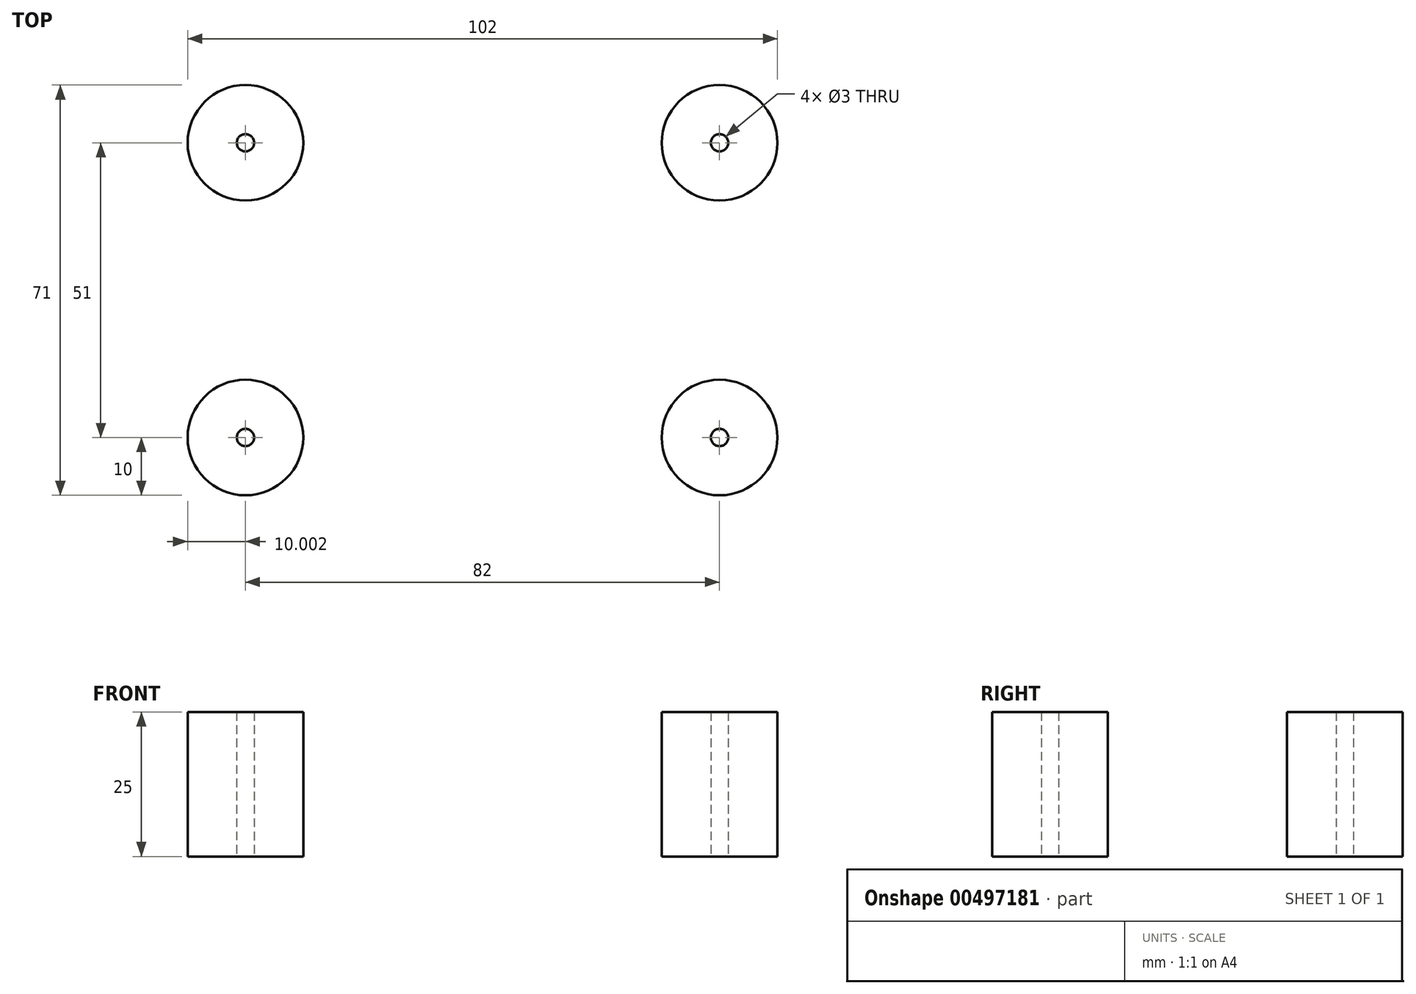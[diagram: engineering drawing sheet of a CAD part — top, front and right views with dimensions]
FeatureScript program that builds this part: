
annotation { "Feature Type Name" : "Feature", "Feature Type Description" : "" }
export const myFeature = defineFeature(function(context is Context, id is Id, definition is map)
    precondition{}
    {
        {
            var Q0;
            Q0=qCreatedBy(makeId("Top.planeOp"),FACE);
            var sketch = newSketch(context, id + "F0", { "sketchPlane" : qUnion([Q0])});
            skLineSegment(sketch, "E0.bottom", {"start": v(-75.58, 100.07) * mm, "end": v(74.42, 100.07) * mm});
            skLineSegment(sketch, "E0.top", {"start": v(-75.58, -99.93) * mm, "end": v(74.42, -99.93) * mm});
            skLineSegment(sketch, "E0.left", {"start": v(-75.58, 100.07) * mm, "end": v(-75.58, -99.93) * mm});
            skLineSegment(sketch, "E0.right", {"start": v(74.42, 100.07) * mm, "end": v(74.42, -99.93) * mm});
            skPoint(sketch, "E0.middle", {"position": v(-0.58, 0.07) * mm});
            skLineSegment(sketch, "E1.bottom", {"start": v(-69.33, 93.82) * mm, "end": v(68.17, 93.82) * mm});
            skLineSegment(sketch, "E1.top", {"start": v(-69.33, -93.68) * mm, "end": v(68.17, -93.68) * mm});
            skLineSegment(sketch, "E1.left", {"start": v(-69.33, 93.82) * mm, "end": v(-69.33, -93.68) * mm});
            skLineSegment(sketch, "E1.right", {"start": v(68.17, 93.82) * mm, "end": v(68.17, -93.68) * mm});
            skLineSegment(sketch, "E2.bottom", {"start": v(-63.08, 87.57) * mm, "end": v(61.92, 87.57) * mm});
            skLineSegment(sketch, "E2.top", {"start": v(-63.08, -87.43) * mm, "end": v(61.92, -87.43) * mm});
            skLineSegment(sketch, "E2.left", {"start": v(-63.08, 87.57) * mm, "end": v(-63.08, -87.43) * mm});
            skLineSegment(sketch, "E2.right", {"start": v(61.92, 87.57) * mm, "end": v(61.92, -87.43) * mm});
            skLineSegment(sketch, "E3.bottom", {"start": v(-51.58, 35.57) * mm, "end": v(50.42, 35.57) * mm, "construction": true});
            skLineSegment(sketch, "E3.top", {"start": v(-51.58, -35.43) * mm, "end": v(50.42, -35.43) * mm, "construction": true});
            skLineSegment(sketch, "E3.left", {"start": v(-51.58, 35.57) * mm, "end": v(-51.58, -35.43) * mm, "construction": true});
            skLineSegment(sketch, "E3.right", {"start": v(50.42, 35.57) * mm, "end": v(50.42, -35.43) * mm, "construction": true});
            skPoint(sketch, "E4", {"position": v(36.92, 87.57) * mm});
            skPoint(sketch, "E5", {"position": v(36.92, -87.43) * mm});
            skPoint(sketch, "E6", {"position": v(-38.08, 87.57) * mm});
            skPoint(sketch, "E7", {"position": v(-38.08, -87.43) * mm});
            skPoint(sketch, "E8", {"position": v(-63.08, 62.57) * mm});
            skPoint(sketch, "E9", {"position": v(61.92, 62.57) * mm});
            skPoint(sketch, "E10", {"position": v(61.92, -62.43) * mm});
            skPoint(sketch, "E11", {"position": v(-63.08, -62.43) * mm});
            skPoint(sketch, "E12", {"position": v(-63.08, 87.57) * mm});
            skPoint(sketch, "E13", {"position": v(61.92, 87.57) * mm});
            skPoint(sketch, "E14", {"position": v(61.92, -87.43) * mm});
            skPoint(sketch, "E15", {"position": v(-63.08, -87.43) * mm});
            skLineSegment(sketch, "E16", {"start": v(-63.08, -62.43) * mm, "end": v(-38.08, -87.43) * mm});
            skLineSegment(sketch, "E17", {"start": v(36.92, -87.43) * mm, "end": v(61.92, -62.43) * mm});
            skLineSegment(sketch, "E18", {"start": v(61.92, 62.57) * mm, "end": v(36.92, 87.57) * mm});
            skLineSegment(sketch, "E19", {"start": v(-38.08, 87.57) * mm, "end": v(-63.08, 62.57) * mm});
            skPoint(sketch, "E20", {"position": v(-50.58, 75.07) * mm});
            skPoint(sketch, "E21", {"position": v(49.42, 75.07) * mm});
            skPoint(sketch, "E22", {"position": v(49.42, -74.93) * mm});
            skPoint(sketch, "E23", {"position": v(-50.58, -74.93) * mm});
            skLineSegment(sketch, "E24", {"start": v(-63.08, 87.57) * mm, "end": v(-50.58, 75.07) * mm, "construction": true});
            skLineSegment(sketch, "E25", {"start": v(61.92, 87.57) * mm, "end": v(49.42, 75.07) * mm, "construction": true});
            skLineSegment(sketch, "E26", {"start": v(61.92, -87.43) * mm, "end": v(49.42, -74.93) * mm, "construction": true});
            skLineSegment(sketch, "E27", {"start": v(-63.08, -87.43) * mm, "end": v(-50.58, -74.93) * mm, "construction": true});
            skPoint(sketch, "E28", {"position": v(-56.83, 81.32) * mm});
            skPoint(sketch, "E29", {"position": v(55.67, 81.32) * mm});
            skPoint(sketch, "E30", {"position": v(55.67, -81.18) * mm});
            skPoint(sketch, "E31", {"position": v(-56.83, -81.18) * mm});
            skLineSegment(sketch, "E32.bottom", {"start": v(-51.58, 35.57) * mm, "end": v(-41.58, 35.57) * mm, "construction": true});
            skLineSegment(sketch, "E32.top", {"start": v(-51.58, 25.57) * mm, "end": v(-41.58, 25.57) * mm, "construction": true});
            skLineSegment(sketch, "E32.left", {"start": v(-51.58, 35.57) * mm, "end": v(-51.58, 25.57) * mm, "construction": true});
            skLineSegment(sketch, "E32.right", {"start": v(-41.58, 35.57) * mm, "end": v(-41.58, 25.57) * mm, "construction": true});
            skLineSegment(sketch, "E33.bottom", {"start": v(50.42, 35.57) * mm, "end": v(40.42, 35.57) * mm, "construction": true});
            skLineSegment(sketch, "E33.top", {"start": v(50.42, 25.57) * mm, "end": v(40.42, 25.57) * mm, "construction": true});
            skLineSegment(sketch, "E33.left", {"start": v(50.42, 35.57) * mm, "end": v(50.42, 25.57) * mm, "construction": true});
            skLineSegment(sketch, "E33.right", {"start": v(40.42, 35.57) * mm, "end": v(40.42, 25.57) * mm, "construction": true});
            skLineSegment(sketch, "E34.bottom", {"start": v(-51.58, -35.43) * mm, "end": v(-41.58, -35.43) * mm, "construction": true});
            skLineSegment(sketch, "E34.top", {"start": v(-51.58, -25.43) * mm, "end": v(-41.58, -25.43) * mm, "construction": true});
            skLineSegment(sketch, "E34.left", {"start": v(-51.58, -35.43) * mm, "end": v(-51.58, -25.43) * mm, "construction": true});
            skLineSegment(sketch, "E34.right", {"start": v(-41.58, -35.43) * mm, "end": v(-41.58, -25.43) * mm, "construction": true});
            skLineSegment(sketch, "E35.bottom", {"start": v(50.42, -35.43) * mm, "end": v(40.42, -35.43) * mm, "construction": true});
            skLineSegment(sketch, "E35.top", {"start": v(50.42, -25.43) * mm, "end": v(40.42, -25.43) * mm, "construction": true});
            skLineSegment(sketch, "E35.left", {"start": v(50.42, -35.43) * mm, "end": v(50.42, -25.43) * mm, "construction": true});
            skLineSegment(sketch, "E35.right", {"start": v(40.42, -35.43) * mm, "end": v(40.42, -25.43) * mm, "construction": true});
            skPoint(sketch, "E36", {"position": v(-41.58, 25.57) * mm});
            skPoint(sketch, "E37", {"position": v(40.42, 25.57) * mm});
            skPoint(sketch, "E38", {"position": v(40.42, -25.43) * mm});
            skPoint(sketch, "E39", {"position": v(-41.58, -25.43) * mm});
            skCircle(sketch, "E40", {"center": v(40.42, 25.57) * mm, "radius": 10 * mm});
            skCircle(sketch, "E41", {"center": v(-41.58, 25.57) * mm, "radius": 10 * mm});
            skCircle(sketch, "E42", {"center": v(-41.58, -25.43) * mm, "radius": 10 * mm});
            skCircle(sketch, "E43", {"center": v(40.42, -25.43) * mm, "radius": 10 * mm});
            skCircle(sketch, "E44", {"center": v(40.42, 25.57) * mm, "radius": 1.5 * mm});
            skCircle(sketch, "E45", {"center": v(-41.58, 25.57) * mm, "radius": 1.5 * mm});
            skCircle(sketch, "E46", {"center": v(-41.58, -25.43) * mm, "radius": 1.5 * mm});
            skCircle(sketch, "E47", {"center": v(40.42, -25.43) * mm, "radius": 1.5 * mm});
            skCircle(sketch, "E48", {"center": v(-0.58, 0.07) * mm, "radius": 10 * mm});
            skCircle(sketch, "E49", {"center": v(-63.08, 87.57) * mm, "radius": 1.5 * mm});
            skCircle(sketch, "E50", {"center": v(61.92, 87.57) * mm, "radius": 1.5 * mm});
            skCircle(sketch, "E51", {"center": v(61.92, -87.43) * mm, "radius": 1.5 * mm});
            skCircle(sketch, "E52", {"center": v(-63.08, -87.43) * mm, "radius": 1.5 * mm});
            skCircle(sketch, "E53", {"center": v(-56.83, -81.18) * mm, "radius": 2.5 * mm});
            skCircle(sketch, "E54", {"center": v(55.67, -81.18) * mm, "radius": 2.5 * mm});
            skCircle(sketch, "E55", {"center": v(55.67, 81.32) * mm, "radius": 2.5 * mm});
            skCircle(sketch, "E56", {"center": v(-56.83, 81.32) * mm, "radius": 2.5 * mm});
            skPoint(sketch, "E57", {"position": v(-0.58, 75.05) * mm});
            skPoint(sketch, "E58", {"position": v(14.42, -87.43) * mm});
            skPoint(sketch, "E59", {"position": v(14.42, -99.93) * mm});
            skPoint(sketch, "E60", {"position": v(-15.58, -99.93) * mm});
            skPoint(sketch, "E61", {"position": v(-15.58, -87.43) * mm});
            skLineSegment(sketch, "E62", {"start": v(-15.58, -87.43) * mm, "end": v(-15.58, -99.93) * mm});
            skLineSegment(sketch, "E63", {"start": v(14.42, -87.43) * mm, "end": v(14.42, -99.93) * mm});
            skPoint(sketch, "E64", {"position": v(31.92, -87.43) * mm});
            skPoint(sketch, "E65", {"position": v(31.92, -99.93) * mm});
            skPoint(sketch, "E66", {"position": v(19.42, -99.93) * mm});
            skPoint(sketch, "E67", {"position": v(19.42, -87.43) * mm});
            skPoint(sketch, "E68", {"position": v(-20.58, -87.43) * mm});
            skPoint(sketch, "E69", {"position": v(-33.08, -87.43) * mm});
            skPoint(sketch, "E70", {"position": v(-33.08, -99.93) * mm});
            skPoint(sketch, "E71", {"position": v(-20.58, -99.93) * mm});
            skPoint(sketch, "E72", {"position": v(-15.58, 87.57) * mm});
            skPoint(sketch, "E73", {"position": v(-20.58, 87.57) * mm});
            skPoint(sketch, "E74", {"position": v(-33.08, 87.57) * mm});
            skPoint(sketch, "E75", {"position": v(31.92, 87.57) * mm});
            skPoint(sketch, "E76", {"position": v(19.42, 87.57) * mm});
            skPoint(sketch, "E77", {"position": v(14.42, 87.57) * mm});
            skPoint(sketch, "E78", {"position": v(-33.08, 100.07) * mm});
            skPoint(sketch, "E79", {"position": v(-20.58, 100.07) * mm});
            skPoint(sketch, "E80", {"position": v(-15.58, 100.07) * mm});
            skPoint(sketch, "E81", {"position": v(14.42, 100.07) * mm});
            skPoint(sketch, "E82", {"position": v(19.42, 100.07) * mm});
            skPoint(sketch, "E83", {"position": v(31.92, 100.07) * mm});
            skPoint(sketch, "E84", {"position": v(74.42, 15.07) * mm});
            skPoint(sketch, "E85", {"position": v(74.42, -14.93) * mm});
            skPoint(sketch, "E86", {"position": v(-75.58, -14.93) * mm});
            skPoint(sketch, "E87", {"position": v(-75.58, 15.07) * mm});
            skPoint(sketch, "E88", {"position": v(61.92, 15.07) * mm});
            skPoint(sketch, "E89", {"position": v(61.92, -14.93) * mm});
            skPoint(sketch, "E90", {"position": v(-63.08, 15.07) * mm});
            skPoint(sketch, "E91", {"position": v(-63.08, -14.93) * mm});
            skLineSegment(sketch, "E92", {"start": v(-33.08, 100.07) * mm, "end": v(-33.08, 87.57) * mm});
            skLineSegment(sketch, "E93", {"start": v(-20.58, 100.07) * mm, "end": v(-20.58, 87.57) * mm});
            skLineSegment(sketch, "E94", {"start": v(-15.58, 100.07) * mm, "end": v(-15.58, 87.57) * mm});
            skLineSegment(sketch, "E95", {"start": v(14.42, 100.07) * mm, "end": v(14.42, 87.57) * mm});
            skLineSegment(sketch, "E96", {"start": v(19.42, 100.07) * mm, "end": v(19.42, 87.57) * mm});
            skLineSegment(sketch, "E97", {"start": v(31.92, 100.07) * mm, "end": v(31.92, 87.57) * mm});
            skLineSegment(sketch, "E98", {"start": v(74.42, 15.07) * mm, "end": v(61.92, 15.07) * mm});
            skLineSegment(sketch, "E99", {"start": v(74.42, -14.93) * mm, "end": v(61.92, -14.93) * mm});
            skLineSegment(sketch, "E100", {"start": v(-63.08, 15.07) * mm, "end": v(-75.58, 15.07) * mm});
            skLineSegment(sketch, "E101", {"start": v(-63.08, -14.93) * mm, "end": v(-75.58, -14.93) * mm});
            skLineSegment(sketch, "E102", {"start": v(-33.08, -87.43) * mm, "end": v(-33.08, -99.93) * mm});
            skLineSegment(sketch, "E103", {"start": v(-20.58, -87.43) * mm, "end": v(-20.58, -99.93) * mm});
            skLineSegment(sketch, "E104", {"start": v(19.42, -87.43) * mm, "end": v(19.42, -99.93) * mm});
            skLineSegment(sketch, "E105", {"start": v(31.92, -87.43) * mm, "end": v(31.92, -99.93) * mm});
            skPoint(sketch, "E106", {"position": v(61.92, 46.07) * mm});
            skPoint(sketch, "E107", {"position": v(61.92, 33.57) * mm});
            skPoint(sketch, "E108", {"position": v(61.92, -45.93) * mm});
            skPoint(sketch, "E109", {"position": v(61.92, -33.43) * mm});
            skPoint(sketch, "E110", {"position": v(-63.08, 46.07) * mm});
            skPoint(sketch, "E111", {"position": v(-63.08, 33.57) * mm});
            skPoint(sketch, "E112", {"position": v(-63.08, -33.43) * mm});
            skPoint(sketch, "E113", {"position": v(-63.08, -45.93) * mm});
            skPoint(sketch, "E114", {"position": v(-75.58, 46.07) * mm});
            skPoint(sketch, "E115", {"position": v(-75.58, 33.57) * mm});
            skPoint(sketch, "E116", {"position": v(-75.58, -33.43) * mm});
            skPoint(sketch, "E117", {"position": v(-75.58, -45.93) * mm});
            skPoint(sketch, "E118", {"position": v(74.42, -45.93) * mm});
            skPoint(sketch, "E119", {"position": v(74.42, -33.43) * mm});
            skPoint(sketch, "E120", {"position": v(74.42, 46.07) * mm});
            skPoint(sketch, "E121", {"position": v(74.42, 33.57) * mm});
            skLineSegment(sketch, "E122", {"start": v(-75.58, 46.07) * mm, "end": v(-63.08, 46.07) * mm});
            skLineSegment(sketch, "E123", {"start": v(-75.58, 33.57) * mm, "end": v(-63.08, 33.57) * mm});
            skLineSegment(sketch, "E124", {"start": v(-75.58, -33.43) * mm, "end": v(-63.08, -33.43) * mm});
            skLineSegment(sketch, "E125", {"start": v(-75.58, -45.93) * mm, "end": v(-63.08, -45.93) * mm});
            skLineSegment(sketch, "E126", {"start": v(61.92, -33.43) * mm, "end": v(74.42, -33.43) * mm});
            skLineSegment(sketch, "E127", {"start": v(61.92, -45.93) * mm, "end": v(74.42, -45.93) * mm});
            skLineSegment(sketch, "E128", {"start": v(61.92, 46.07) * mm, "end": v(74.42, 46.07) * mm});
            skPoint(sketch, "E129", {"position": v(-33.08, 93.82) * mm});
            skPoint(sketch, "E130", {"position": v(-20.58, 93.82) * mm});
            skPoint(sketch, "E131", {"position": v(-15.58, 93.82) * mm});
            skPoint(sketch, "E132", {"position": v(14.42, 93.82) * mm});
            skPoint(sketch, "E133", {"position": v(19.42, 93.82) * mm});
            skPoint(sketch, "E134", {"position": v(31.92, 93.82) * mm});
            skPoint(sketch, "E135", {"position": v(68.17, 46.07) * mm});
            skPoint(sketch, "E136", {"position": v(68.17, 33.57) * mm});
            skPoint(sketch, "E137", {"position": v(68.17, 15.07) * mm});
            skPoint(sketch, "E138", {"position": v(68.17, -14.93) * mm});
            skPoint(sketch, "E139", {"position": v(68.17, -33.43) * mm});
            skPoint(sketch, "E140", {"position": v(68.17, -45.93) * mm});
            skPoint(sketch, "E141", {"position": v(31.92, -93.68) * mm});
            skPoint(sketch, "E142", {"position": v(19.42, -93.68) * mm});
            skPoint(sketch, "E143", {"position": v(14.42, -93.68) * mm});
            skPoint(sketch, "E144", {"position": v(-15.58, -93.68) * mm});
            skPoint(sketch, "E145", {"position": v(-20.58, -93.68) * mm});
            skPoint(sketch, "E146", {"position": v(-33.08, -93.68) * mm});
            skPoint(sketch, "E147", {"position": v(-69.33, -45.93) * mm});
            skPoint(sketch, "E148", {"position": v(-69.33, -33.43) * mm});
            skPoint(sketch, "E149", {"position": v(-69.33, -14.93) * mm});
            skPoint(sketch, "E150", {"position": v(-69.33, 15.07) * mm});
            skPoint(sketch, "E151", {"position": v(-69.33, 33.57) * mm});
            skPoint(sketch, "E152", {"position": v(-69.33, 46.07) * mm});
            skLineSegment(sketch, "E153", {"start": v(74.42, 33.57) * mm, "end": v(61.92, 33.57) * mm});
            skSolve(sketch);
        }
        {
            var Q0;
            Q0=makeQuery(id+"F0.imprint","IMPRINT",FACE,{"disambiguationData":[TD([[makeQuery(id+"F0.imprint","IMPRINT",EDGE,{"derivedFrom":sQuery(id+"F0.wireOp",EDGE,"E41")}),1.0]])]});
            var Q1;
            Q1=makeQuery(id+"F0.imprint","IMPRINT",FACE,{"disambiguationData":[TD([[makeQuery(id+"F0.imprint","IMPRINT",EDGE,{"derivedFrom":sQuery(id+"F0.wireOp",EDGE,"E40")}),1.0]])]});
            var Q2;
            Q2=makeQuery(id+"F0.imprint","IMPRINT",FACE,{"disambiguationData":[TD([[makeQuery(id+"F0.imprint","IMPRINT",EDGE,{"derivedFrom":sQuery(id+"F0.wireOp",EDGE,"E43")}),1.0]])]});
            var Q3;
            Q3=makeQuery(id+"F0.imprint","IMPRINT",FACE,{"disambiguationData":[TD([[makeQuery(id+"F0.imprint","IMPRINT",EDGE,{"derivedFrom":sQuery(id+"F0.wireOp",EDGE,"E42")}),1.0]])]});
            extrude(context, id + "F1", {"entities" : qUnion([Q0, Q1, Q2, Q3]), "depth" : 25 * mm});
        }
    });
